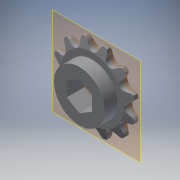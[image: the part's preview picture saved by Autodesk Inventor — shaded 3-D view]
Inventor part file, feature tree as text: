
AUTODESK INVENTOR PART (.ipt)
format: ipt  version: 2017 (Build 210142000, 142)  size: 374,272 bytes
history: native  units: in
note: dims shown in document units (in); Inventor stores cm internally (conversion verified against a paired STEP export)
features: plane x1, other x1
ambient origin geometry x8: Origin, YZ Plane, XZ Plane, XY Plane, X Axis, Y Axis, Z Axis, Center Point
bodies: Solid1 (feature_tree)
feature tree (2):
  plane  "Work Plane1"
  other  "Cut-Extrude3"
